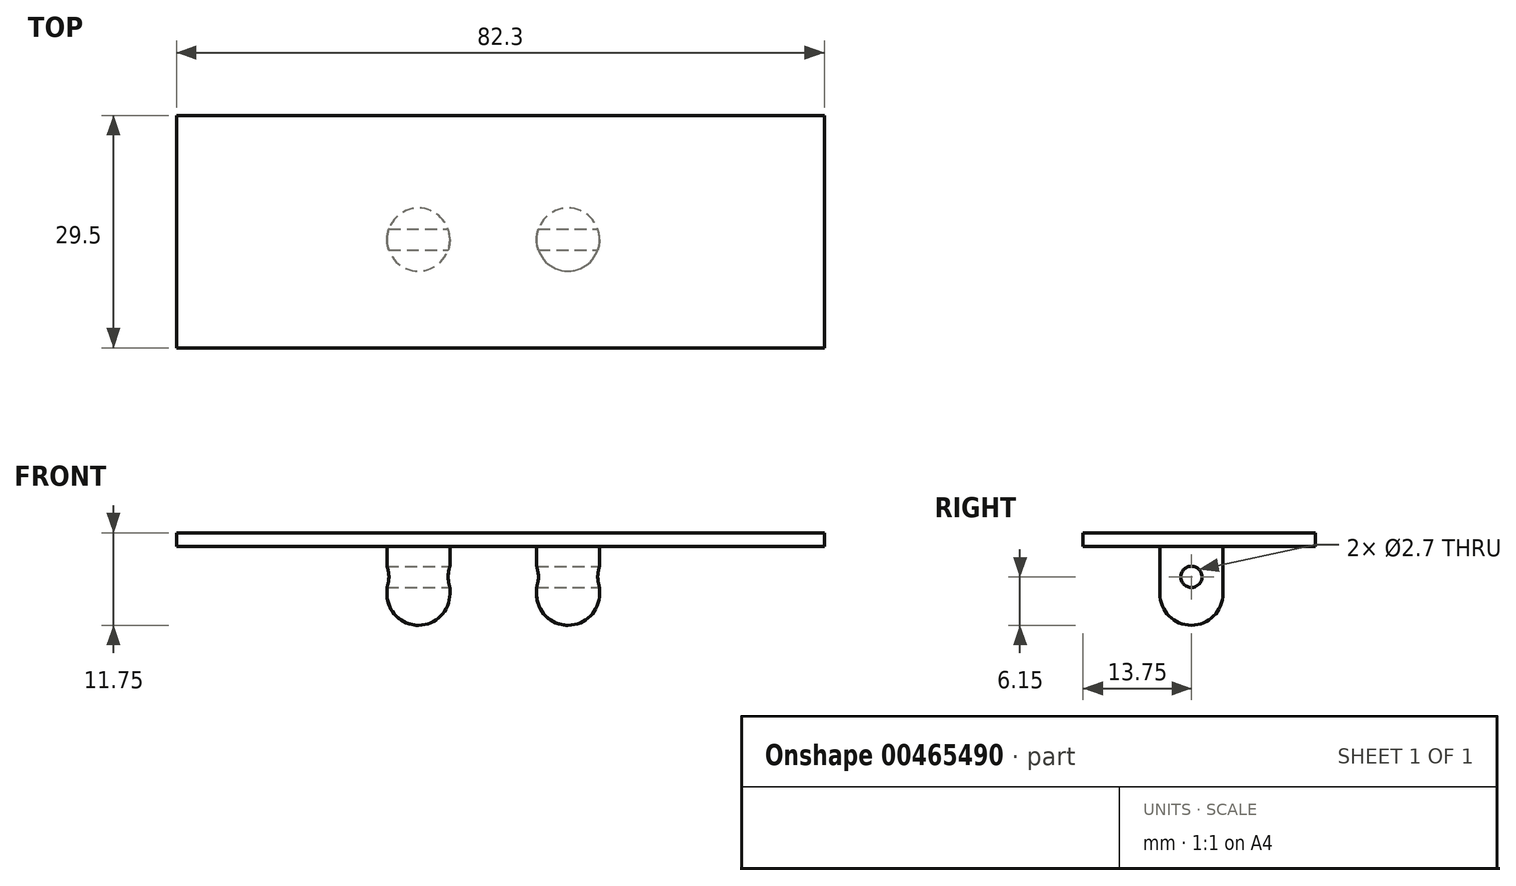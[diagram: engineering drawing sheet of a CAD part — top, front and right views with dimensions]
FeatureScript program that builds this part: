
annotation { "Feature Type Name" : "Feature", "Feature Type Description" : "" }
export const myFeature = defineFeature(function(context is Context, id is Id, definition is map)
    precondition{}
    {
        {
            var Q0;
            Q0=qCreatedBy(makeId("Top.planeOp"),FACE);
            var sketch = newSketch(context, id + "F0", { "sketchPlane" : qUnion([Q0])});
            skLineSegment(sketch, "E0.bottom", {"start": v(0, 0) * mm, "end": v(-88, 0) * mm});
            skLineSegment(sketch, "E0.top", {"start": v(0, 37) * mm, "end": v(-88, 37) * mm});
            skLineSegment(sketch, "E0.left", {"start": v(0, 0) * mm, "end": v(0, 37) * mm});
            skLineSegment(sketch, "E0.right", {"start": v(-88, 0) * mm, "end": v(-88, 37) * mm});
            skSolve(sketch);
        }
        {
            var Q0;
            Q0=qSketchRegion(id+"F0",true);
            extrude(context, id + "F1", {"entities" : qUnion([Q0]), "depth" : 1.75 * mm, "offsetDistance" : 25 * mm});
        }
        {
            var Q0;
            Q0=makeQuery(id+"F1.opExtrude","CAP_FACE",FACE,{"disambiguationData":[OSD([sQuery(id+"F0.wireOp",EDGE,"E0.bottom"),sQuery(id+"F0.wireOp",EDGE,"E0.top"),sQuery(id+"F0.wireOp",EDGE,"E0.left"),sQuery(id+"F0.wireOp",EDGE,"E0.right")])],"isStart":false});
            var sketch = newSketch(context, id + "F2", { "sketchPlane" : qUnion([Q0])});
            skLineSegment(sketch, "E1.bottom", {"start": v(-84.25, 33.25) * mm, "end": v(-1.95, 33.25) * mm});
            skLineSegment(sketch, "E1.top", {"start": v(-84.25, 3.75) * mm, "end": v(-1.95, 3.75) * mm});
            skLineSegment(sketch, "E1.left", {"start": v(-84.25, 33.25) * mm, "end": v(-84.25, 3.75) * mm});
            skLineSegment(sketch, "E1.right", {"start": v(-1.95, 33.25) * mm, "end": v(-1.95, 3.75) * mm});
            skSolve(sketch);
        }
        {
            var Q0;
            Q0=qSketchRegion(id+"F2",true);
            extrude(context, id + "F3", {"entities" : qUnion([Q0]), "operationType" : NewBodyOperationType.ADD, "depth" : 1.5 * mm, "offsetDistance" : 25 * mm});
        }
        {
            var Q0;
            Q0=makeQuery(id+"F1.opExtrude","CAP_FACE",FACE,{"disambiguationData":[OSD([sQuery(id+"F0.wireOp",EDGE,"E0.bottom"),sQuery(id+"F0.wireOp",EDGE,"E0.top"),sQuery(id+"F0.wireOp",EDGE,"E0.left"),sQuery(id+"F0.wireOp",EDGE,"E0.right")])],"isStart":true});
            var sketch = newSketch(context, id + "F4", { "sketchPlane" : qUnion([Q0])});
            skCircle(sketch, "E2", {"center": v(-53.5, -17.5) * mm, "radius": 4 * mm});
            skLineSegment(sketch, "E3", {"start": v(-44, 0) * mm, "end": v(-44, -37) * mm, "construction": true});
            skCircle(sketch, "E4.MirrorC", {"center": v(-34.5, -17.5) * mm, "radius": 4 * mm});
            skSolve(sketch);
        }
        {
            var Q0;
            Q0=qSketchRegion(id+"F4",true);
            extrude(context, id + "F5", {"entities" : qUnion([Q0]), "operationType" : NewBodyOperationType.ADD, "depth" : 10 * mm});
        }
        {
            var Q0;
            Q0=makeQuery(id+"F5.opExtrude","CAP_EDGE",EDGE,{"disambiguationData":[OSD([sQuery(id+"F4.wireOp",EDGE,"E2")])],"isStart":false});
            var Q1;
            Q1=makeQuery(id+"F5.opExtrude","CAP_EDGE",EDGE,{"disambiguationData":[OSD([sQuery(id+"F4.wireOp",EDGE,"E4.MirrorC")])],"isStart":false});
            fillet(context, id + "F6", {"entities" : qUnion([Q0, Q1]), "radius" : 4 * mm, "tangentPropagation" : true, "allowEdgeOverflow" : false});
        }
        {
            var Q0;
            Q0=makeQuery(id+"F52yH6P0KQi80XE_1.boolean.opBoolean","MERGE",FACE,{"derivedFrom":[makeQuery(id+"F1.opExtrude","SWEPT_FACE",FACE,{"disambiguationData":[OSD([sQuery(id+"F0.wireOp",EDGE,"E0.left")])]}),makeQuery(id+"F52yH6P0KQi80XE_1.opExtrude","SWEPT_FACE",FACE,{"disambiguationData":[OSD([sQuery(id+"FGr434h4xjwXrtd_1.wireOp",EDGE,"zj5YKJeh-aPVd-Q5X6-8lwT-vVkT89wnBvyn.right")])]})]});
            var sketch = newSketch(context, id + "F7", { "sketchPlane" : qUnion([Q0])});
            skCircle(sketch, "E5", {"center": v(17.5, -3.85) * mm, "radius": 1.35 * mm});
            skSolve(sketch);
        }
        {
            var Q0;
            Q0=qSketchRegion(id+"F7",true);
            extrude(context, id + "F8", {"entities" : qUnion([Q0]), "operationType" : NewBodyOperationType.REMOVE, "endBound" : BoundingType.THROUGH_ALL, "oppositeDirection" : true, "depth" : 25 * mm});
        }
        {
            var Q0;
            Q0=makeQuery(id+"F1.opExtrude","SWEPT_EDGE",EDGE,{"disambiguationData":[OSD([sQuery(id+"F0.wireOp",EDGE,"E0.bottom"),sQuery(id+"F0.wireOp",EDGE,"E0.right")])]});
            var Q1;
            Q1=makeQuery(id+"F1.opExtrude","SWEPT_EDGE",EDGE,{"disambiguationData":[OSD([sQuery(id+"F0.wireOp",EDGE,"E0.top"),sQuery(id+"F0.wireOp",EDGE,"E0.right")])]});
            var Q2;
            Q2=makeQuery(id+"F1.opExtrude","SWEPT_EDGE",EDGE,{"disambiguationData":[OSD([sQuery(id+"F0.wireOp",EDGE,"E0.top"),sQuery(id+"F0.wireOp",EDGE,"E0.left")])]});
            var Q3;
            Q3=makeQuery(id+"F1.opExtrude","SWEPT_EDGE",EDGE,{"disambiguationData":[OSD([sQuery(id+"F0.wireOp",EDGE,"E0.bottom"),sQuery(id+"F0.wireOp",EDGE,"E0.left")])]});
            fillet(context, id + "F9", {"entities" : qUnion([Q0, Q1, Q2, Q3]), "radius" : 3 * mm, "tangentPropagation" : true, "allowEdgeOverflow" : false});
        }
        {
            var Q0;
            Q0=qSketchRegion(id+"F2",true);
            extrude(context, id + "F10", {"entities" : qUnion([Q0]), "operationType" : NewBodyOperationType.INTERSECT, "oppositeDirection" : true, "depth" : 25 * mm, "offsetDistance" : 25 * mm});
        }
    });
